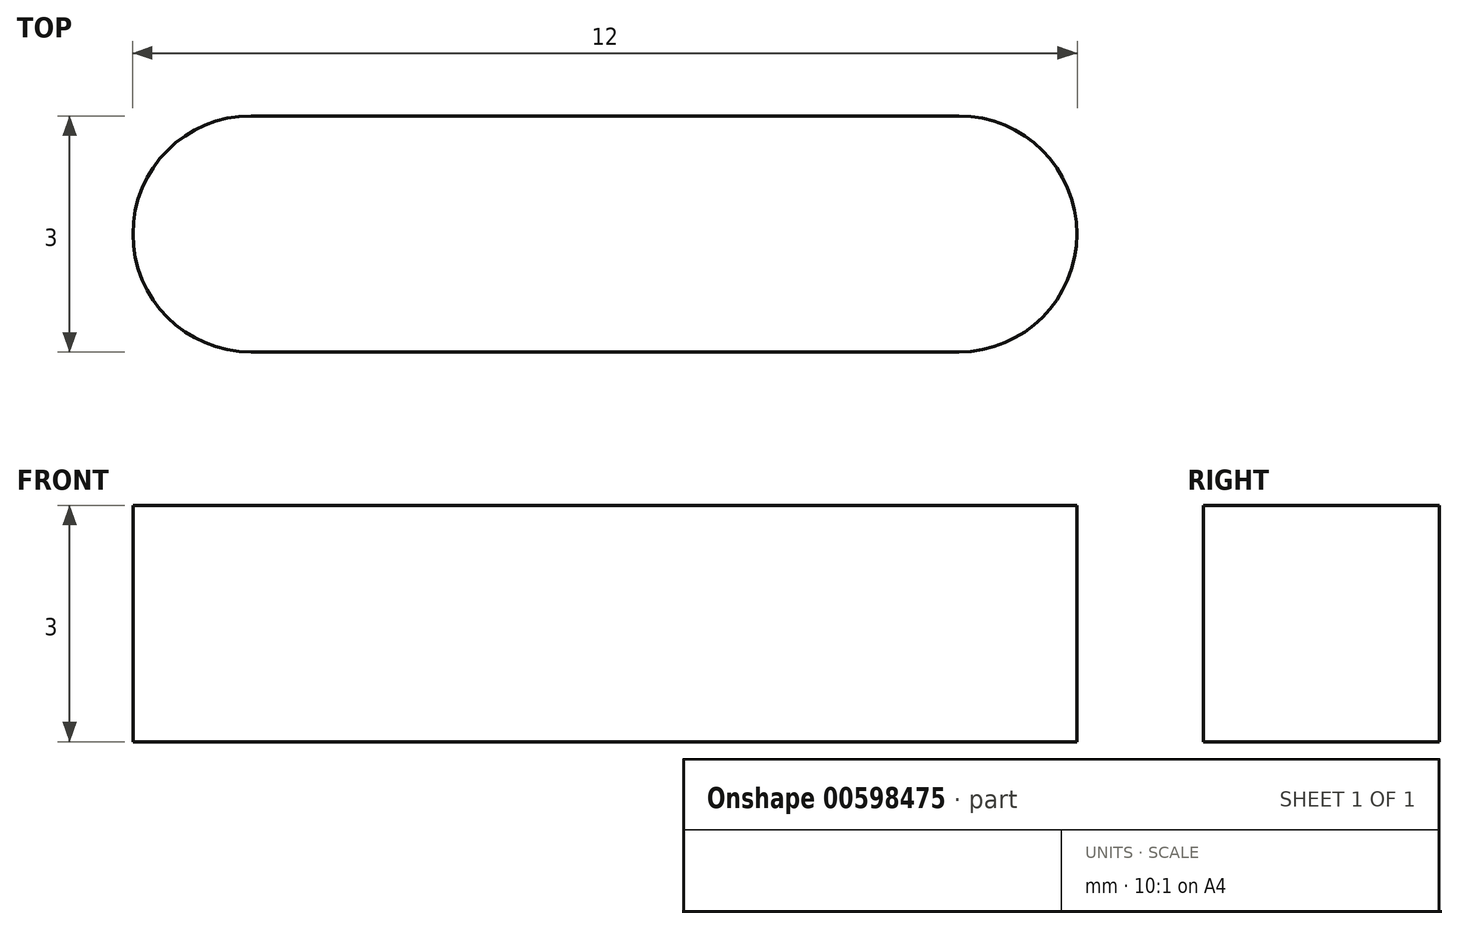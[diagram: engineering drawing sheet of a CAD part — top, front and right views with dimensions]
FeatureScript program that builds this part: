
annotation { "Feature Type Name" : "Feature", "Feature Type Description" : "" }
export const myFeature = defineFeature(function(context is Context, id is Id, definition is map)
    precondition{}
    {
        {
            var Q0;
            Q0=qCreatedBy(makeId("Top.planeOp"),FACE);
            var sketch = newSketch(context, id + "F0", { "sketchPlane" : qUnion([Q0])});
            skLineSegment(sketch, "E0.bottom", {"start": v(4.5, 1.5) * mm, "end": v(-4.5, 1.5) * mm});
            skLineSegment(sketch, "E0.top", {"start": v(4.5, -1.5) * mm, "end": v(-4.5, -1.5) * mm});
            skPoint(sketch, "E0.middle", {"position": v(0, 0) * mm});
            skArc(sketch, "E1", {"start": v(-4.5, 1.5) * mm, "mid": v(-6, 0) * mm, "end": v(-4.5, -1.5) * mm});
            skArc(sketch, "E2", {"start": v(4.5, -1.5) * mm, "mid": v(6, 0) * mm, "end": v(4.5, 1.5) * mm});
            skSolve(sketch);
        }
        {
            var Q0;
            Q0=makeQuery(id+"F0.imprint","IMPRINT",FACE,{"disambiguationData":[TD([[makeQuery(id+"F0.imprint","IMPRINT",EDGE,{"derivedFrom":sQuery(id+"F0.wireOp",EDGE,"E0.bottom")}),1.0]])]});
            extrude(context, id + "F1", {"entities" : qUnion([Q0]), "depth" : 3 * mm, "offsetDistance" : 25.4 * mm});
        }
    });
